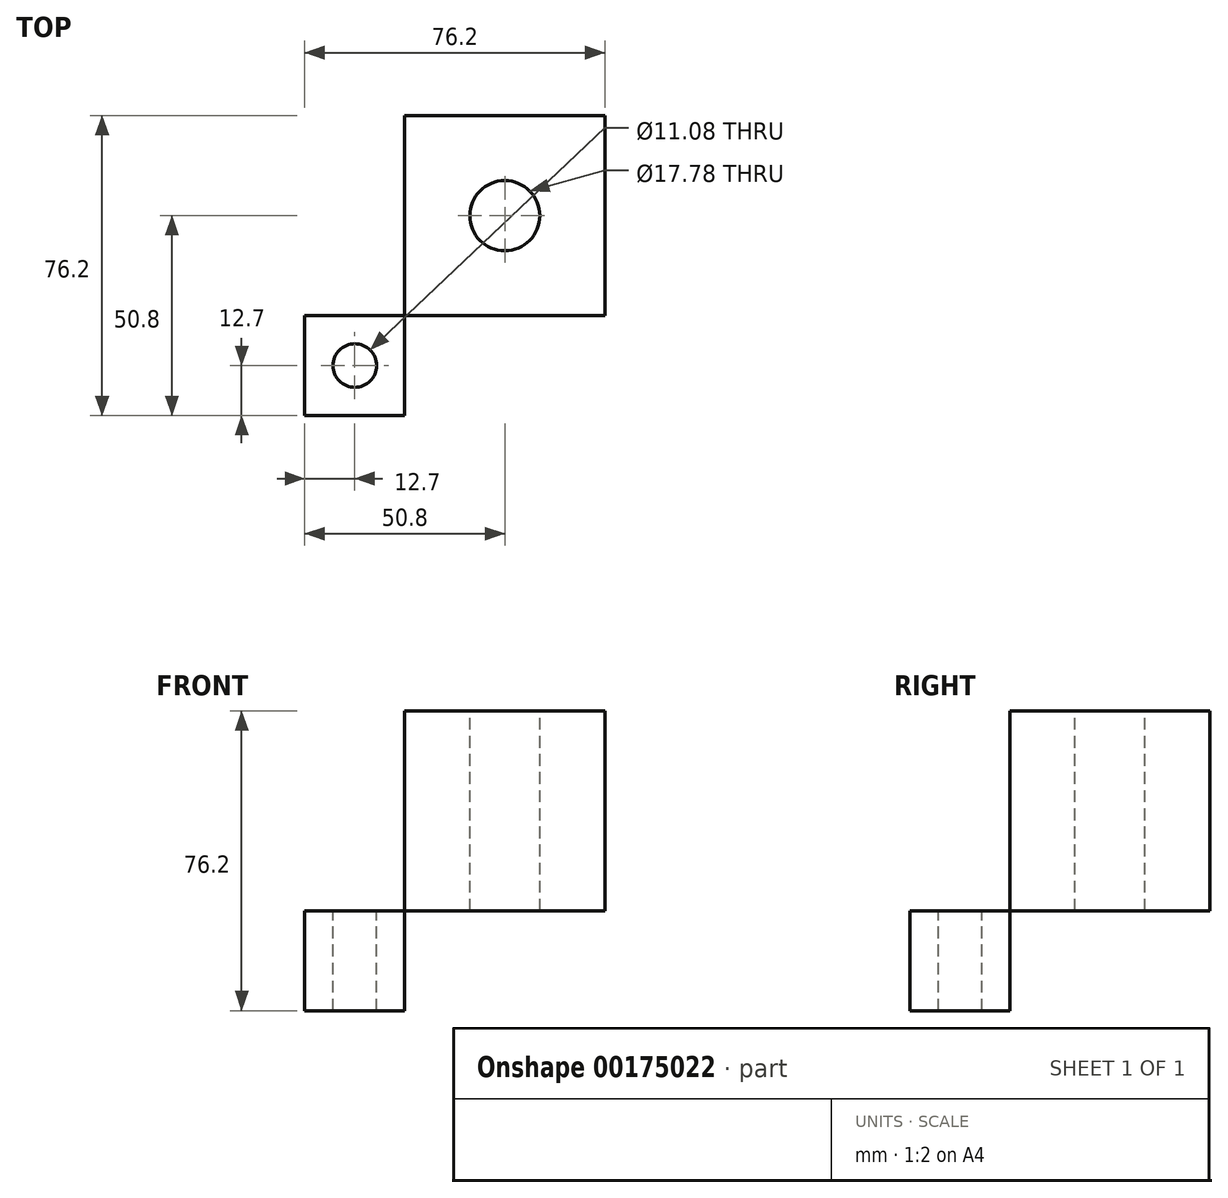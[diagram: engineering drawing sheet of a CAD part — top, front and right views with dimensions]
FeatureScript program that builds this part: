
annotation { "Feature Type Name" : "Feature", "Feature Type Description" : "" }
export const myFeature = defineFeature(function(context is Context, id is Id, definition is map)
    precondition{}
    {
        {
            var Q0;
            Q0=qCreatedBy(makeId("Front.planeOp"),FACE);
            var sketch = newSketch(context, id + "F0", { "sketchPlane" : qUnion([Q0])});
            skLineSegment(sketch, "E0.bottom", {"start": v(0, 0) * mm, "end": v(50.8, 0) * mm});
            skLineSegment(sketch, "E0.top", {"start": v(0, 50.8) * mm, "end": v(50.8, 50.8) * mm});
            skLineSegment(sketch, "E0.left", {"start": v(0, 0) * mm, "end": v(0, 50.8) * mm});
            skLineSegment(sketch, "E0.right", {"start": v(50.8, 0) * mm, "end": v(50.8, 50.8) * mm});
            skSolve(sketch);
        }
        {
            var Q0;
            Q0=makeQuery(id+"F0.imprint","IMPRINT",FACE,{"disambiguationData":[TD([[makeQuery(id+"F0.imprint","IMPRINT",EDGE,{"derivedFrom":sQuery(id+"F0.wireOp",EDGE,"E0.bottom")}),1.0]])]});
            extrude(context, id + "F1", {"entities" : qUnion([Q0]), "depth" : 50.8 * mm});
        }
        {
            var Q0;
            Q0=makeQuery(id+"F1.opExtrude","CAP_FACE",FACE,{"disambiguationData":[OSD([sQuery(id+"F0.wireOp",EDGE,"E0.bottom"),sQuery(id+"F0.wireOp",EDGE,"E0.top"),sQuery(id+"F0.wireOp",EDGE,"E0.left"),sQuery(id+"F0.wireOp",EDGE,"E0.right")])],"isStart":false});
            var sketch = newSketch(context, id + "F2", { "sketchPlane" : qUnion([Q0])});
            skLineSegment(sketch, "E1.bottom", {"start": v(0, 0) * mm, "end": v(-25.4, 0) * mm});
            skLineSegment(sketch, "E1.top", {"start": v(0, -25.4) * mm, "end": v(-25.4, -25.4) * mm});
            skLineSegment(sketch, "E1.left", {"start": v(0, 0) * mm, "end": v(0, -25.4) * mm});
            skLineSegment(sketch, "E1.right", {"start": v(-25.4, 0) * mm, "end": v(-25.4, -25.4) * mm});
            skSolve(sketch);
        }
        {
            var Q0;
            Q0 = qSketchRegion(id + "F2", true);
            extrude(context, id + "F3", {"entities" : qUnion([Q0]), "depth" : 25.4 * mm});
        }
        {
            var Q0;
            Q0=makeQuery(id+"F1.opExtrude","SWEPT_FACE",FACE,{"disambiguationData":[OSD([sQuery(id+"F0.wireOp",EDGE,"E0.top")])]});
            var sketch = newSketch(context, id + "F4", { "sketchPlane" : qUnion([Q0])});
            skCircle(sketch, "E2", {"center": v(25.4, -25.4) * mm, "radius": 8.9 * mm});
            skSolve(sketch);
        }
        {
            var Q0;
            Q0 = qSketchRegion(id + "F4", true);
            extrude(context, id + "F5", {"entities" : qUnion([Q0]), "operationType" : NewBodyOperationType.REMOVE, "oppositeDirection" : true, "depth" : 50.8 * mm});
        }
        {
            var Q0;
            Q0=makeQuery(id+"F3.opExtrude","SWEPT_FACE",FACE,{"disambiguationData":[OSD([sQuery(id+"F2.wireOp",EDGE,"E1.bottom")])]});
            var sketch = newSketch(context, id + "F6", { "sketchPlane" : qUnion([Q0])});
            skCircle(sketch, "E3", {"center": v(-12.7, -63.5) * mm, "radius": 5.54 * mm});
            skPoint(sketch, "E3.centerSnap0", {"position": v(0, -63.5) * mm});
            skSolve(sketch);
        }
        {
            var Q0;
            Q0 = qSketchRegion(id + "F6", true);
            extrude(context, id + "F7", {"entities" : qUnion([Q0]), "operationType" : NewBodyOperationType.REMOVE, "oppositeDirection" : true, "depth" : 25.4 * mm});
        }
    });
